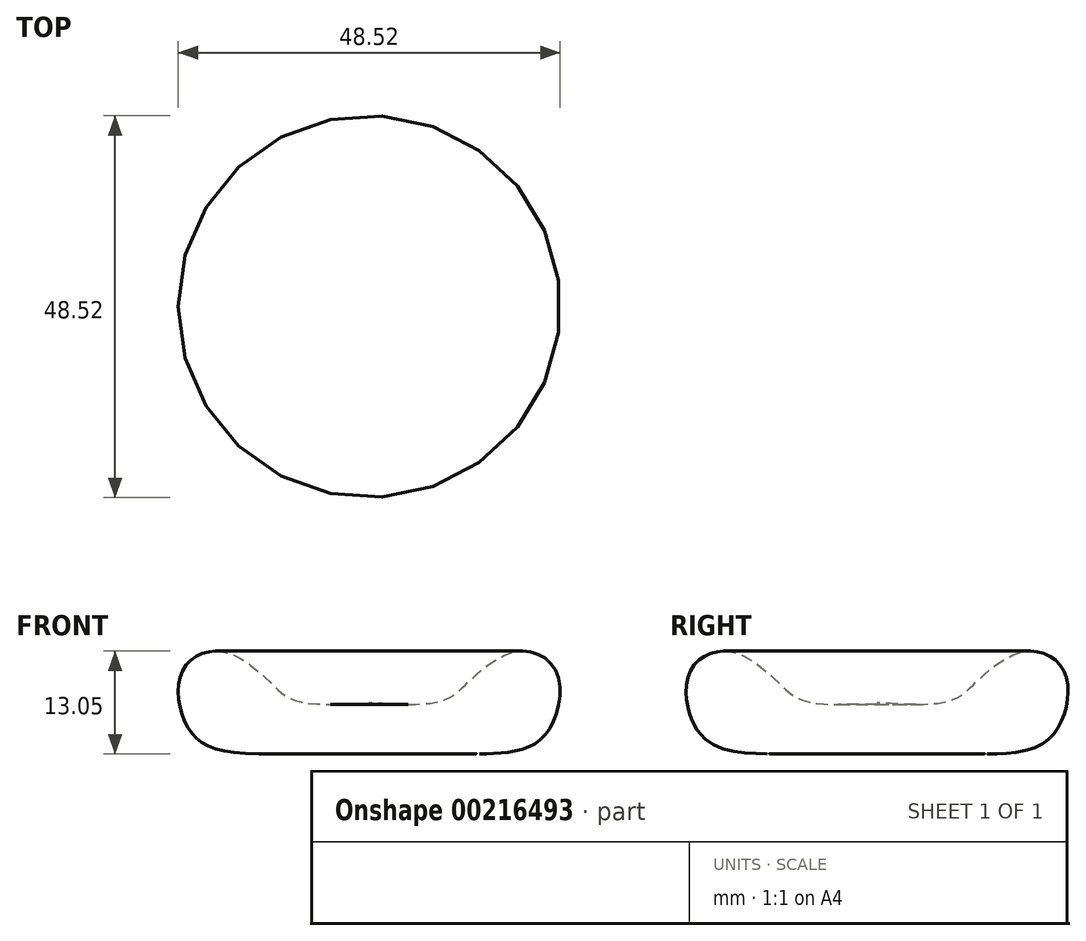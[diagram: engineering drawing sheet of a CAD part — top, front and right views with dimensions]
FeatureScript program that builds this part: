
annotation { "Feature Type Name" : "Feature", "Feature Type Description" : "" }
export const myFeature = defineFeature(function(context is Context, id is Id, definition is map)
    precondition{}
    {
        {
            var Q0;
            Q0=qCreatedBy(makeId("Front.planeOp"),FACE);
            var sketch = newSketch(context, id + "F0", { "sketchPlane" : qUnion([Q0])});
            skLineSegment(sketch, "E0", {"start": v(0, 0) * mm, "end": v(-14, 0) * mm});
            skFitSpline(sketch, "E1", {"points": [v(-14, 0) * mm, v(-23.06, 3.41) * mm, v(-23.71, 10.54) * mm, v(-18.65, 12.98) * mm, v(-12.16, 8.7) * mm, v(0, 6.48) * mm], "startDerivative": vector(-76.6, 0) * mm, "endDerivative": vector(113.8, 7.93) * mm});
            skLineSegment(sketch, "E2", {"start": v(0, 12.77) * mm, "end": v(0, -5.68) * mm, "construction": true});
            skSolve(sketch);
        }
        {
            var Q0;
            Q0=sQuery(id+"F0.wireOp",EDGE,"E1");
            var Q1;
            Q1=sQuery(id+"F0.wireOp",EDGE,"E0");
            var Q2;
            Q2=sQuery(id+"F0.wireOp",EDGE,"E2");
            revolve(context, id + "F1", {"bodyType" : ToolBodyType.SURFACE, "surfaceEntities" : qUnion([Q0, Q1]), "axis" : qUnion([Q2]), "revolveType" : RevolveType.FULL});
        }
    });
